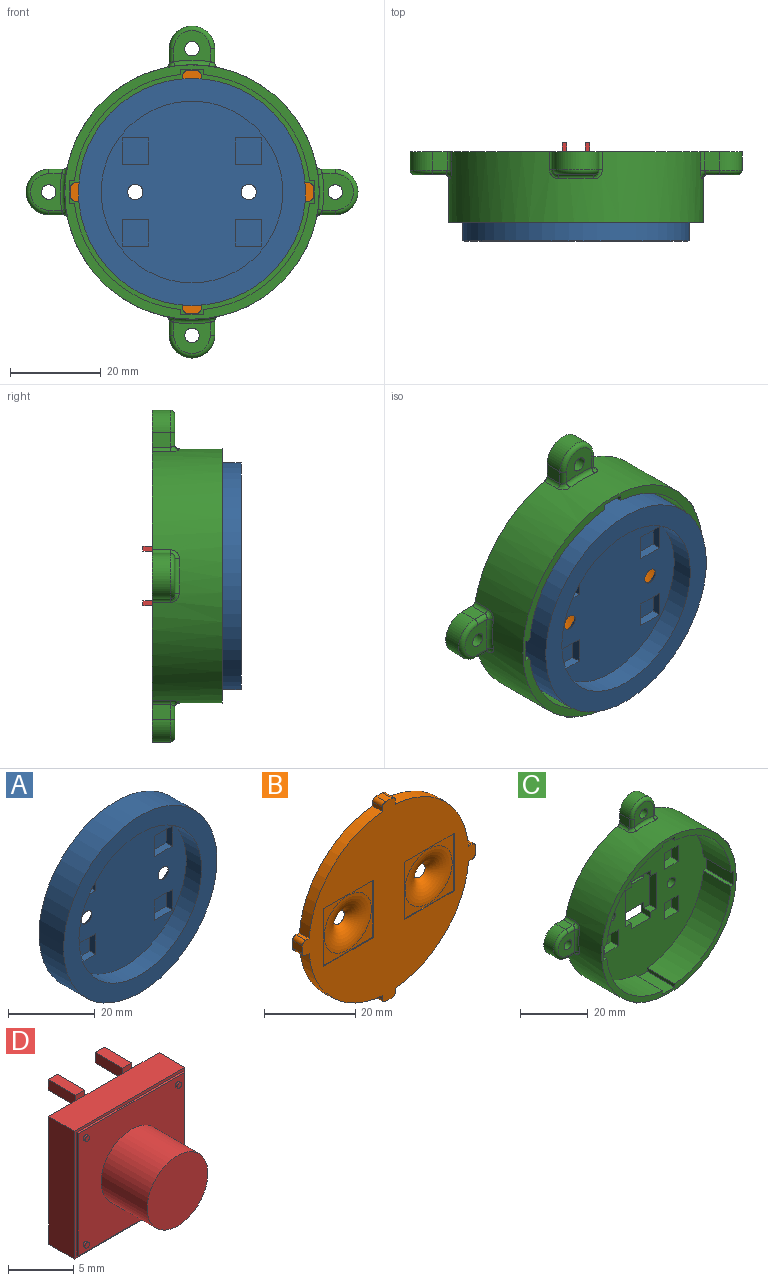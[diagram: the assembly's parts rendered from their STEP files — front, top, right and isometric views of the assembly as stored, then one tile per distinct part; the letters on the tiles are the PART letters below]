
ASSEMBLY  parts=4 mates=3
PART A: 37 faces, bbox 50x8x50 mm
  f0: plane 50x50mm, normal (0,1,0), area 1489.2mm2, adj f2,f25,f26,f27,f28,f30,f31,f32
  f1: plane 40x40mm, normal (0,-1,0), area 1103.9mm2, adj f3,f5,f6,f7,f8,f10,f11,f12
  f2: cylinder r=25mm len=50mm, axis (0,1,0), area 1256.6mm2, adj f0,f4
  f3: cylinder r=20mm len=40mm, axis (0,1,0), area 628.3mm2, adj f1,f4
  f4: plane 50x50mm, normal (0,-1,0), area 706.9mm2, adj f2,f3
  f5: plane 5.8x2mm, normal (0,0,1), area 11.6mm2, adj f1,f6,f8,f9
  f6: plane 5.8x2mm, normal (-1,0,0), area 11.6mm2, adj f1,f5,f7,f9
  f7: plane 5.8x2mm, normal (0,0,-1), area 11.6mm2, adj f1,f6,f8,f9
  f8: plane 5.8x2mm, normal (1,0,0), area 11.6mm2, adj f1,f5,f7,f9
  f9: plane 5.8x5.8mm, normal (0,-1,0), area 33.6mm2, adj f5,f6,f7,f8
  f10: plane 5.8x2mm, normal (0,0,1), area 11.6mm2, adj f1,f11,f13,f14
  f11: plane 5.8x2mm, normal (-1,0,0), area 11.6mm2, adj f1,f10,f12,f14
  f12: plane 5.8x2mm, normal (0,0,-1), area 11.6mm2, adj f1,f11,f13,f14
  f13: plane 5.8x2mm, normal (1,0,0), area 11.6mm2, adj f1,f10,f12,f14
  f14: plane 5.8x5.8mm, normal (0,-1,0), area 33.6mm2, adj f10,f11,f12,f13
  f15: plane 5.8x2mm, normal (0,0,1), area 11.6mm2, adj f1,f16,f18,f19
  f16: plane 5.8x2mm, normal (-1,0,0), area 11.6mm2, adj f1,f15,f17,f19
  f17: plane 5.8x2mm, normal (0,0,-1), area 11.6mm2, adj f1,f16,f18,f19
  f18: plane 5.8x2mm, normal (1,0,0), area 11.6mm2, adj f1,f15,f17,f19
  f19: plane 5.8x5.8mm, normal (0,-1,0), area 33.6mm2, adj f15,f16,f17,f18
  f20: plane 5.8x2mm, normal (0,0,1), area 11.6mm2, adj f1,f21,f23,f24
  f21: plane 5.8x2mm, normal (-1,0,0), area 11.6mm2, adj f1,f20,f22,f24
  f22: plane 5.8x2mm, normal (0,0,-1), area 11.6mm2, adj f1,f21,f23,f24
  f23: plane 5.8x2mm, normal (1,0,0), area 11.6mm2, adj f1,f20,f22,f24
  f24: plane 5.8x5.8mm, normal (0,-1,0), area 33.6mm2, adj f20,f21,f22,f23
  f25: plane 15.4x0.2mm, normal (0,0,-1), area 3.1mm2, adj f0,f26,f28,f29
  f26: plane 15.4x0.2mm, normal (-1,0,0), area 3.1mm2, adj f0,f25,f27,f29
  f27: plane 15.4x0.2mm, normal (0,0,1), area 3.1mm2, adj f0,f26,f28,f29
  f28: plane 15.4x0.2mm, normal (1,0,0), area 3.1mm2, adj f0,f25,f27,f29
  f29: plane 15.4x15.4mm, normal (0,1,0), area 69.7mm2, adj f25,f26,f27,f28,f35
  f30: plane 15.4x0.2mm, normal (0,0,-1), area 3.1mm2, adj f0,f31,f33,f34
  f31: plane 15.4x0.2mm, normal (-1,0,0), area 3.1mm2, adj f0,f30,f32,f34
  f32: plane 15.4x0.2mm, normal (0,0,1), area 3.1mm2, adj f0,f31,f33,f34
  f33: plane 15.4x0.2mm, normal (1,0,0), area 3.1mm2, adj f0,f30,f32,f34
  f34: plane 15.4x15.4mm, normal (0,1,0), area 69.7mm2, adj f30,f31,f32,f33,f36
  f35: torus R=7.3mm, axis (0,1,0), area 174.6mm2, adj f1,f29
  f36: torus R=7.3mm, axis (0,1,0), area 174.6mm2, adj f1,f34
PART B: 58 faces, bbox 53.5x7.2x53.5 mm
  f0: plane 53.5x53.5mm, normal (0,-1,0), area 1480.7mm2, adj f2,f3,f4,f5,f6,f7,f8,f9
  f1: plane 53.5x53.5mm, normal (0,1,0), area 1802.3mm2, adj f2,f3,f4,f5,f6,f7,f8,f9
  f2: cylinder r=24.75mm len=22.67mm, axis (0,1,0), area 104.6mm2, adj f0,f1,f9,f10
  f3: cylinder r=24.75mm len=22.67mm, axis (0,1,0), area 104.6mm2, adj f0,f1,f6,f14
  f4: plane 3x1.08mm, normal (0,0,1), area 3.2mm2, adj f0,f1,f13,f50
  f5: plane 3x2mm, normal (-1,0,0), area 6mm2, adj f0,f1,f50,f51
  f6: plane 3x1.08mm, normal (0,0,-1), area 3.2mm2, adj f0,f1,f3,f51
  f7: plane 3x1.08mm, normal (0,0,-1), area 3.2mm2, adj f0,f1,f17,f52
  f8: plane 3x2mm, normal (1,0,0), area 6mm2, adj f0,f1,f52,f53
  f9: plane 3x1.08mm, normal (0,0,1), area 3.2mm2, adj f0,f1,f2,f53
  f10: plane 3x1.08mm, normal (1,0,0), area 3.2mm2, adj f0,f1,f2,f54
  f11: plane 3x2mm, normal (0,0,1), area 6mm2, adj f0,f1,f54,f55
  f12: plane 3x1.08mm, normal (-1,0,0), area 3.2mm2, adj f0,f1,f13,f55
  f13: cylinder r=24.75mm len=22.67mm, axis (0,1,0), area 104.6mm2, adj f0,f1,f4,f12
  f14: plane 3x1.08mm, normal (-1,0,0), area 3.2mm2, adj f0,f1,f3,f56
  f15: plane 3x2mm, normal (0,0,-1), area 6mm2, adj f0,f1,f56,f57
  f16: plane 3x1.08mm, normal (1,0,0), area 3.2mm2, adj f0,f1,f17,f57
  f17: cylinder r=24.75mm len=22.67mm, axis (0,1,0), area 104.6mm2, adj f0,f1,f7,f16
  f18: plane 5.8x2mm, normal (0,0,-1), area 11.6mm2, adj f1,f19,f21,f22
  f19: plane 5.8x2mm, normal (-1,0,0), area 11.6mm2, adj f1,f18,f20,f22
  f20: plane 5.8x2mm, normal (0,0,1), area 11.6mm2, adj f1,f19,f21,f22
  f21: plane 5.8x2mm, normal (1,0,0), area 11.6mm2, adj f1,f18,f20,f22
  f22: plane 5.8x5.8mm, normal (0,1,0), area 33.6mm2, adj f18,f19,f20,f21
  f23: plane 5.8x2mm, normal (0,0,-1), area 11.6mm2, adj f1,f24,f26,f27
  f24: plane 5.8x2mm, normal (-1,0,0), area 11.6mm2, adj f1,f23,f25,f27
  f25: plane 5.8x2mm, normal (0,0,1), area 11.6mm2, adj f1,f24,f26,f27
  f26: plane 5.8x2mm, normal (1,0,0), area 11.6mm2, adj f1,f23,f25,f27
  f27: plane 5.8x5.8mm, normal (0,1,0), area 33.6mm2, adj f23,f24,f25,f26
  f28: plane 5.8x2mm, normal (0,0,-1), area 11.6mm2, adj f1,f29,f31,f32
  f29: plane 5.8x2mm, normal (-1,0,0), area 11.6mm2, adj f1,f28,f30,f32
  f30: plane 5.8x2mm, normal (0,0,1), area 11.6mm2, adj f1,f29,f31,f32
  f31: plane 5.8x2mm, normal (1,0,0), area 11.6mm2, adj f1,f28,f30,f32
  f32: plane 5.8x5.8mm, normal (0,1,0), area 33.6mm2, adj f28,f29,f30,f31
  f33: plane 5.8x2mm, normal (0,0,-1), area 11.6mm2, adj f1,f34,f36,f37
  f34: plane 5.8x2mm, normal (-1,0,0), area 11.6mm2, adj f1,f33,f35,f37
  f35: plane 5.8x2mm, normal (0,0,1), area 11.6mm2, adj f1,f34,f36,f37
  f36: plane 5.8x2mm, normal (1,0,0), area 11.6mm2, adj f1,f33,f35,f37
  f37: plane 5.8x5.8mm, normal (0,1,0), area 33.6mm2, adj f33,f34,f35,f36
  f38: plane 15.4x0.2mm, normal (0,0,-1), area 3.1mm2, adj f0,f39,f41,f42
  f39: plane 15.4x0.2mm, normal (1,0,0), area 3.1mm2, adj f0,f38,f40,f42
  f40: plane 15.4x0.2mm, normal (0,0,1), area 3.1mm2, adj f0,f39,f41,f42
  f41: plane 15.4x0.2mm, normal (-1,0,0), area 3.1mm2, adj f0,f38,f40,f42
  f42: plane 15.4x15.4mm, normal (0,-1,0), area 69.7mm2, adj f38,f39,f40,f41,f48
  f43: plane 15.4x0.2mm, normal (0,0,-1), area 3.1mm2, adj f0,f44,f46,f47
  f44: plane 15.4x0.2mm, normal (1,0,0), area 3.1mm2, adj f0,f43,f45,f47
  f45: plane 15.4x0.2mm, normal (0,0,1), area 3.1mm2, adj f0,f44,f46,f47
  f46: plane 15.4x0.2mm, normal (-1,0,0), area 3.1mm2, adj f0,f43,f45,f47
  f47: plane 15.4x15.4mm, normal (0,-1,0), area 69.7mm2, adj f43,f44,f45,f46,f49
  f48: torus R=7.3mm, axis (0,-1,0), area 174.6mm2, adj f1,f42
  f49: torus R=7.3mm, axis (0,-1,0), area 174.6mm2, adj f1,f47
  f50: cylinder r=1mm len=3mm, axis (0,1,0), area 4.7mm2, adj f0,f1,f4,f5
  f51: cylinder r=1mm len=3mm, axis (0,-1,0), area 4.7mm2, adj f0,f1,f5,f6
  f52: cylinder r=1mm len=3mm, axis (0,-1,0), area 4.7mm2, adj f0,f1,f7,f8
  f53: cylinder r=1mm len=3mm, axis (0,1,0), area 4.7mm2, adj f0,f1,f8,f9
  f54: cylinder r=1mm len=3mm, axis (0,1,0), area 4.7mm2, adj f0,f1,f10,f11
  f55: cylinder r=1mm len=3mm, axis (0,-1,0), area 4.7mm2, adj f0,f1,f11,f12
  f56: cylinder r=1mm len=3mm, axis (0,-1,0), area 4.7mm2, adj f0,f1,f14,f15
  f57: cylinder r=1mm len=3mm, axis (0,1,0), area 4.7mm2, adj f0,f1,f15,f16
PART C: 109 faces, bbox 73.9x15.5x73.9 mm
  f0: plane 54.16x54.16mm, normal (0,-1,0), area 1792.4mm2, adj f2,f3,f4,f5,f6,f7,f8,f9
  f1: cylinder r=28mm len=56mm, axis (0,1,0), area 2453.6mm2, adj f15,f20,f57,f59,f61,f63,f64,f65
  f2: cylinder r=26mm len=23.38mm, axis (0,1,0), area 412.1mm2, adj f0,f3,f15,f35
  f3: plane 11.5x1.2mm, normal (0,0,-1), area 13.8mm2, adj f0,f2,f5,f15
  f4: plane 11.5x1.2mm, normal (0,0,1), area 13.8mm2, adj f0,f5,f6,f15
  f5: plane 11.5x5mm, normal (-1,0,0), area 57.5mm2, adj f0,f3,f4,f15
  f6: cylinder r=26mm len=23.38mm, axis (0,1,0), area 412.1mm2, adj f0,f4,f7,f15
  f7: plane 11.5x1.2mm, normal (-1,0,0), area 13.8mm2, adj f0,f6,f9,f15
  f8: plane 11.5x1.2mm, normal (1,0,0), area 13.8mm2, adj f0,f9,f10,f15
  f9: plane 11.5x5mm, normal (0,0,1), area 57.5mm2, adj f0,f7,f8,f15
  f10: cylinder r=26mm len=23.38mm, axis (0,1,0), area 412.1mm2, adj f0,f8,f11,f15
  f11: plane 11.5x1.2mm, normal (0,0,1), area 13.8mm2, adj f0,f10,f13,f15
  f12: plane 11.5x1.2mm, normal (0,0,-1), area 13.8mm2, adj f0,f13,f14,f15
  f13: plane 11.5x5mm, normal (1,0,0), area 57.5mm2, adj f0,f11,f12,f15
  f14: cylinder r=26mm len=23.38mm, axis (0,1,0), area 412.1mm2, adj f0,f12,f15,f34
  f15: plane 56x56mm, normal (0,-1,0), area 316.9mm2, adj f1,f2,f3,f4,f5,f6,f7,f8
  f16: plane 8x1mm, normal (0,0,-1), area 8mm2, adj f20,f23,f24,f33
  f17: plane 8x1mm, normal (0,0,1), area 8mm2, adj f18,f19,f20,f33
  f18: plane 4x4mm, normal (-1,0,0), area 10mm2, adj f0,f17,f20,f26,f29,f33
  f19: plane 4x4mm, normal (1,0,0), area 10mm2, adj f0,f17,f20,f26,f30,f33
  f20: plane 73.1x73.1mm, normal (0,1,0), area 2654.8mm2, adj f1,f16,f17,f18,f19,f21,f22,f23
  f21: cylinder r=1.7mm len=4mm, axis (0,1,0), area 42.7mm2, adj f0,f20
  f22: cylinder r=1.7mm len=4mm, axis (0,1,0), area 42.7mm2, adj f0,f20
  f23: plane 4x4mm, normal (-1,0,0), area 10mm2, adj f0,f16,f20,f25,f27,f33
  f24: plane 4x4mm, normal (1,0,0), area 10mm2, adj f0,f16,f20,f25,f32,f33
  f25: plane 8x4mm, normal (0,0,1), area 32mm2, adj f0,f20,f23,f24
  f26: plane 8x4mm, normal (0,0,-1), area 32mm2, adj f0,f18,f19,f20
  f27: plane 3x2.5mm, normal (0,0,1), area 7.5mm2, adj f0,f23,f28,f33
  f28: plane 13x3mm, normal (-1,0,0), area 39mm2, adj f0,f27,f29,f33
  f29: plane 3x2.5mm, normal (0,0,-1), area 7.5mm2, adj f0,f18,f28,f33
  f30: plane 3x2.5mm, normal (0,0,-1), area 7.5mm2, adj f0,f19,f31,f33
  f31: plane 13x3mm, normal (1,0,0), area 39mm2, adj f0,f30,f32,f33
  f32: plane 3x2.5mm, normal (0,0,1), area 7.5mm2, adj f0,f24,f31,f33
  f33: plane 13x13mm, normal (0,-1,0), area 137mm2, adj f16,f17,f18,f19,f23,f24,f27,f28
  f34: plane 11.5x1.2mm, normal (1,0,0), area 13.8mm2, adj f0,f14,f15,f36
  f35: plane 11.5x1.2mm, normal (-1,0,0), area 13.8mm2, adj f0,f2,f15,f36
  f36: plane 11.5x5mm, normal (0,0,-1), area 57.5mm2, adj f0,f15,f34,f35
  f37: plane 4x3.18mm, normal (0,0,-1), area 12.7mm2, adj f20,f38,f70,f72
  f38: cylinder r=5mm len=10mm, axis (0,1,0), area 62.8mm2, adj f20,f37,f39,f68
  f39: plane 4x3.18mm, normal (0,0,1), area 12.7mm2, adj f20,f38,f65,f66
  f40: cylinder r=1.6mm len=5mm, axis (0,1,0), area 50.3mm2, adj f20,f41
  f41: plane 8x6.83mm, normal (0,-1,0), area 38.2mm2, adj f40,f66,f68,f69,f70
  f42: plane 4x3.18mm, normal (1,0,0), area 12.7mm2, adj f20,f43,f78,f80
  f43: cylinder r=5mm len=10mm, axis (0,1,0), area 62.8mm2, adj f20,f42,f44,f76
  f44: plane 4x3.18mm, normal (-1,0,0), area 12.7mm2, adj f20,f43,f73,f74
  f45: cylinder r=1.6mm len=5mm, axis (0,1,0), area 50.3mm2, adj f20,f46
  f46: plane 8x6.83mm, normal (0,-1,0), area 38.2mm2, adj f45,f74,f76,f77,f78
  f47: plane 4x3.18mm, normal (0,0,1), area 12.7mm2, adj f20,f48,f86,f88
  f48: cylinder r=5mm len=10mm, axis (0,1,0), area 62.8mm2, adj f20,f47,f49,f84
  f49: plane 4x3.18mm, normal (0,0,-1), area 12.7mm2, adj f20,f48,f81,f82
  f50: cylinder r=1.6mm len=5mm, axis (0,1,0), area 50.3mm2, adj f20,f51
  f51: plane 8x6.83mm, normal (0,-1,0), area 38.2mm2, adj f50,f82,f84,f85,f86
  f52: plane 4x3.18mm, normal (-1,0,0), area 12.7mm2, adj f20,f53,f62,f64
  f53: cylinder r=5mm len=10mm, axis (0,1,0), area 62.8mm2, adj f20,f52,f54,f60
  f54: plane 4x3.18mm, normal (1,0,0), area 12.7mm2, adj f20,f53,f57,f58
  f55: cylinder r=1.6mm len=5mm, axis (0,1,0), area 50.3mm2, adj f20,f56
  f56: plane 8x6.83mm, normal (0,-1,0), area 38.2mm2, adj f55,f58,f60,f61,f62
  f57: cylinder r=1mm len=4mm, axis (0,1,0), area 5.4mm2, adj f1,f20,f54,f59
  f58: cylinder r=1mm len=3.18mm, axis (0,0,-1), area 4.8mm2, adj f54,f56,f59,f60
  f59: bspline ~2.36x2.04mm, area 3.2mm2, adj f1,f57,f58,f61
  f60: torus R=4mm, axis (0,-1,0), area 22.9mm2, adj f53,f56,f58,f62
  f61: torus R=29mm, axis (0,-1,0), area 12.3mm2, adj f1,f56,f59,f63
  f62: cylinder r=1mm len=3.18mm, axis (0,0,1), area 4.8mm2, adj f52,f56,f60,f63
  f63: bspline ~2.44x2.24mm, area 3.2mm2, adj f1,f61,f62,f64
  f64: cylinder r=1mm len=4mm, axis (0,1,0), area 5.4mm2, adj f1,f20,f52,f63
  f65: cylinder r=1mm len=4mm, axis (0,1,0), area 5.4mm2, adj f1,f20,f39,f67
  f66: cylinder r=1mm len=3.18mm, axis (1,0,0), area 4.8mm2, adj f39,f41,f67,f68
  f67: bspline ~2.36x2.04mm, area 3.2mm2, adj f1,f65,f66,f69
  f68: torus R=4mm, axis (0,-1,0), area 22.9mm2, adj f38,f41,f66,f70
  f69: torus R=29mm, axis (0,-1,0), area 12.3mm2, adj f1,f41,f67,f71
  f70: cylinder r=1mm len=3.18mm, axis (-1,0,0), area 4.8mm2, adj f37,f41,f68,f71
  f71: bspline ~2.44x2.24mm, area 3.2mm2, adj f1,f69,f70,f72
  f72: cylinder r=1mm len=4mm, axis (0,1,0), area 5.4mm2, adj f1,f20,f37,f71
  f73: cylinder r=1mm len=4mm, axis (0,1,0), area 5.4mm2, adj f1,f20,f44,f75
  f74: cylinder r=1mm len=3.18mm, axis (0,0,1), area 4.8mm2, adj f44,f46,f75,f76
  f75: bspline ~2.37x2.36mm, area 3.2mm2, adj f1,f73,f74,f77
  f76: torus R=4mm, axis (0,-1,0), area 22.9mm2, adj f43,f46,f74,f78
  f77: torus R=29mm, axis (0,-1,0), area 12.3mm2, adj f1,f46,f75,f79
  f78: cylinder r=1mm len=3.18mm, axis (0,0,-1), area 4.8mm2, adj f42,f46,f76,f79
  f79: bspline ~2.44x2.24mm, area 3.2mm2, adj f1,f77,f78,f80
  f80: cylinder r=1mm len=4mm, axis (0,1,0), area 5.4mm2, adj f1,f20,f42,f79
  f81: cylinder r=1mm len=4mm, axis (0,1,0), area 5.4mm2, adj f1,f20,f49,f83
  f82: cylinder r=1mm len=3.18mm, axis (-1,0,0), area 4.8mm2, adj f49,f51,f83,f84
  f83: bspline ~2.37x2.36mm, area 3.2mm2, adj f1,f81,f82,f85
  f84: torus R=4mm, axis (0,-1,0), area 22.9mm2, adj f48,f51,f82,f86
  f85: torus R=29mm, axis (0,-1,0), area 12.3mm2, adj f1,f51,f83,f87
  f86: cylinder r=1mm len=3.18mm, axis (1,0,0), area 4.8mm2, adj f47,f51,f84,f87
  f87: bspline ~2.44x2.24mm, area 3.2mm2, adj f1,f85,f86,f88
  f88: cylinder r=1mm len=4mm, axis (0,1,0), area 5.4mm2, adj f1,f20,f47,f87
  f89: plane 5.8x3mm, normal (0,0,-1), area 17.4mm2, adj f0,f90,f92,f93
  f90: plane 5.8x3mm, normal (1,0,0), area 17.4mm2, adj f0,f89,f91,f93
  f91: plane 5.8x3mm, normal (0,0,1), area 17.4mm2, adj f0,f90,f92,f93
  f92: plane 5.8x3mm, normal (-1,0,0), area 17.4mm2, adj f0,f89,f91,f93
  f93: plane 5.8x5.8mm, normal (0,-1,0), area 33.6mm2, adj f89,f90,f91,f92
  f94: plane 5.8x3mm, normal (0,0,-1), area 17.4mm2, adj f0,f95,f97,f98
  f95: plane 5.8x3mm, normal (1,0,0), area 17.4mm2, adj f0,f94,f96,f98
  f96: plane 5.8x3mm, normal (0,0,1), area 17.4mm2, adj f0,f95,f97,f98
  f97: plane 5.8x3mm, normal (-1,0,0), area 17.4mm2, adj f0,f94,f96,f98
  f98: plane 5.8x5.8mm, normal (0,-1,0), area 33.6mm2, adj f94,f95,f96,f97
  f99: plane 5.8x3mm, normal (0,0,-1), area 17.4mm2, adj f0,f100,f102,f103
  f100: plane 5.8x3mm, normal (1,0,0), area 17.4mm2, adj f0,f99,f101,f103
  f101: plane 5.8x3mm, normal (0,0,1), area 17.4mm2, adj f0,f100,f102,f103
  f102: plane 5.8x3mm, normal (-1,0,0), area 17.4mm2, adj f0,f99,f101,f103
  f103: plane 5.8x5.8mm, normal (0,-1,0), area 33.6mm2, adj f99,f100,f101,f102
  f104: plane 5.8x3mm, normal (0,0,-1), area 17.4mm2, adj f0,f105,f107,f108
  f105: plane 5.8x3mm, normal (1,0,0), area 17.4mm2, adj f0,f104,f106,f108
  f106: plane 5.8x3mm, normal (0,0,1), area 17.4mm2, adj f0,f105,f107,f108
  f107: plane 5.8x3mm, normal (-1,0,0), area 17.4mm2, adj f0,f104,f106,f108
  f108: plane 5.8x5.8mm, normal (0,-1,0), area 33.6mm2, adj f104,f105,f106,f107
PART D: 45 faces, bbox 12x11x13 mm
  f0: plane 12x12mm, normal (0,1,0), area 142mm2, adj f17,f18,f19,f20,f22,f23,f24,f27
  f1: plane 11.5x11.5mm, normal (0,-1,0), area 97.3mm2, adj f2,f4,f6,f8,f10,f12,f13,f14
  f2: cylinder r=3.3mm len=6.6mm, axis (0,1,0), area 103.7mm2, adj f1,f3
  f3: plane 6.6x6.6mm, normal (0,-1,0), area 34.2mm2, adj f2
  f4: cylinder r=0.25mm len=0.5mm, axis (0,1,0), area 0.3mm2, adj f1,f5
  f5: plane 0.5x0.5mm, normal (0,-1,0), area 0.2mm2, adj f4
  f6: cylinder r=0.25mm len=0.5mm, axis (0,1,0), area 0.3mm2, adj f1,f7
  f7: plane 0.5x0.5mm, normal (0,-1,0), area 0.2mm2, adj f6
  f8: cylinder r=0.25mm len=0.5mm, axis (0,1,0), area 0.3mm2, adj f1,f9
  f9: plane 0.5x0.5mm, normal (0,-1,0), area 0.2mm2, adj f8
  f10: cylinder r=0.25mm len=0.5mm, axis (0,1,0), area 0.3mm2, adj f1,f11
  f11: plane 0.5x0.5mm, normal (0,-1,0), area 0.2mm2, adj f10
  f12: plane 11.5x0.2mm, normal (-1,0,0), area 2.3mm2, adj f1,f13,f15,f16
  f13: plane 11.5x0.2mm, normal (0,0,1), area 2.3mm2, adj f1,f12,f14,f16
  f14: plane 11.5x0.2mm, normal (1,0,0), area 2.3mm2, adj f1,f13,f15,f16
  f15: plane 11.5x0.2mm, normal (0,0,-1), area 2.3mm2, adj f1,f12,f14,f16
  f16: plane 12x12mm, normal (0,-1,0), area 11.8mm2, adj f12,f13,f14,f15,f17,f18,f19,f20
  f17: plane 12x2.8mm, normal (-1,0,0), area 33.6mm2, adj f0,f16,f18,f20
  f18: plane 12x2.8mm, normal (0,0,1), area 33.6mm2, adj f0,f16,f17,f19,f26,f32
  f19: plane 12x2.8mm, normal (1,0,0), area 33.6mm2, adj f0,f16,f18,f20
  f20: plane 12x2.8mm, normal (0,0,-1), area 33.6mm2, adj f0,f16,f17,f19,f33,f39
  f21: plane 3x1mm, normal (0,0,1), area 3mm2, adj f22,f24,f25,f26
  f22: plane 3x1mm, normal (1,0,0), area 3mm2, adj f0,f21,f23,f25,f26
  f23: plane 3x1mm, normal (0,0,-1), area 3mm2, adj f0,f22,f24,f25
  f24: plane 3x1mm, normal (-1,0,0), area 3mm2, adj f0,f21,f23,f25,f26
  f25: plane 1x1mm, normal (0,1,0), area 1mm2, adj f21,f22,f23,f24
  f26: plane 1x0.5mm, normal (0,-1,0), area 0.5mm2, adj f18,f21,f22,f24
  f27: plane 3x1mm, normal (0,0,-1), area 3mm2, adj f0,f28,f30,f31
  f28: plane 3x1mm, normal (-1,0,0), area 3mm2, adj f0,f27,f29,f31,f32
  f29: plane 3x1mm, normal (0,0,1), area 3mm2, adj f28,f30,f31,f32
  f30: plane 3x1mm, normal (1,0,0), area 3mm2, adj f0,f27,f29,f31,f32
  f31: plane 1x1mm, normal (0,1,0), area 1mm2, adj f27,f28,f29,f30
  f32: plane 1x0.5mm, normal (0,-1,0), area 0.5mm2, adj f18,f28,f29,f30
  f33: plane 1x0.5mm, normal (0,-1,0), area 0.5mm2, adj f20,f34,f35,f36
  f34: plane 3x1mm, normal (1,0,0), area 3mm2, adj f0,f33,f35,f37,f38
  f35: plane 3x1mm, normal (0,0,-1), area 3mm2, adj f33,f34,f36,f38
  f36: plane 3x1mm, normal (-1,0,0), area 3mm2, adj f0,f33,f35,f37,f38
  f37: plane 3x1mm, normal (0,0,1), area 3mm2, adj f0,f34,f36,f38
  f38: plane 1x1mm, normal (0,1,0), area 1mm2, adj f34,f35,f36,f37
  f39: plane 1x0.5mm, normal (0,-1,0), area 0.5mm2, adj f20,f40,f41,f42
  f40: plane 3x1mm, normal (1,0,0), area 3mm2, adj f0,f39,f41,f43,f44
  f41: plane 3x1mm, normal (0,0,-1), area 3mm2, adj f39,f40,f42,f44
  f42: plane 3x1mm, normal (-1,0,0), area 3mm2, adj f0,f39,f41,f43,f44
  f43: plane 3x1mm, normal (0,0,1), area 3mm2, adj f0,f40,f42,f44
  f44: plane 1x1mm, normal (0,1,0), area 1mm2, adj f40,f41,f42,f43
PLACE A t=(-85.19,-43.38,28.97)mm
PLACE B t=(-38.55,-40.78,12.53)mm
PLACE C t=(-126.91,-31.78,28.97)mm
PLACE D t=(-96.31,-32.78,16.4)mm
MATE fastened D.f2 <-> C.f2  axis (0,1,0) through (-85.19,-32.78,28.97)mm
MATE fastened A.f36 <-> B.f48  axis (0,1,0) through (-72.69,-43.58,28.97)mm
MATE fastened D.f2 <-> B.f2  axis (0,-1,0) through (-85.19,-40.78,28.97)mm
